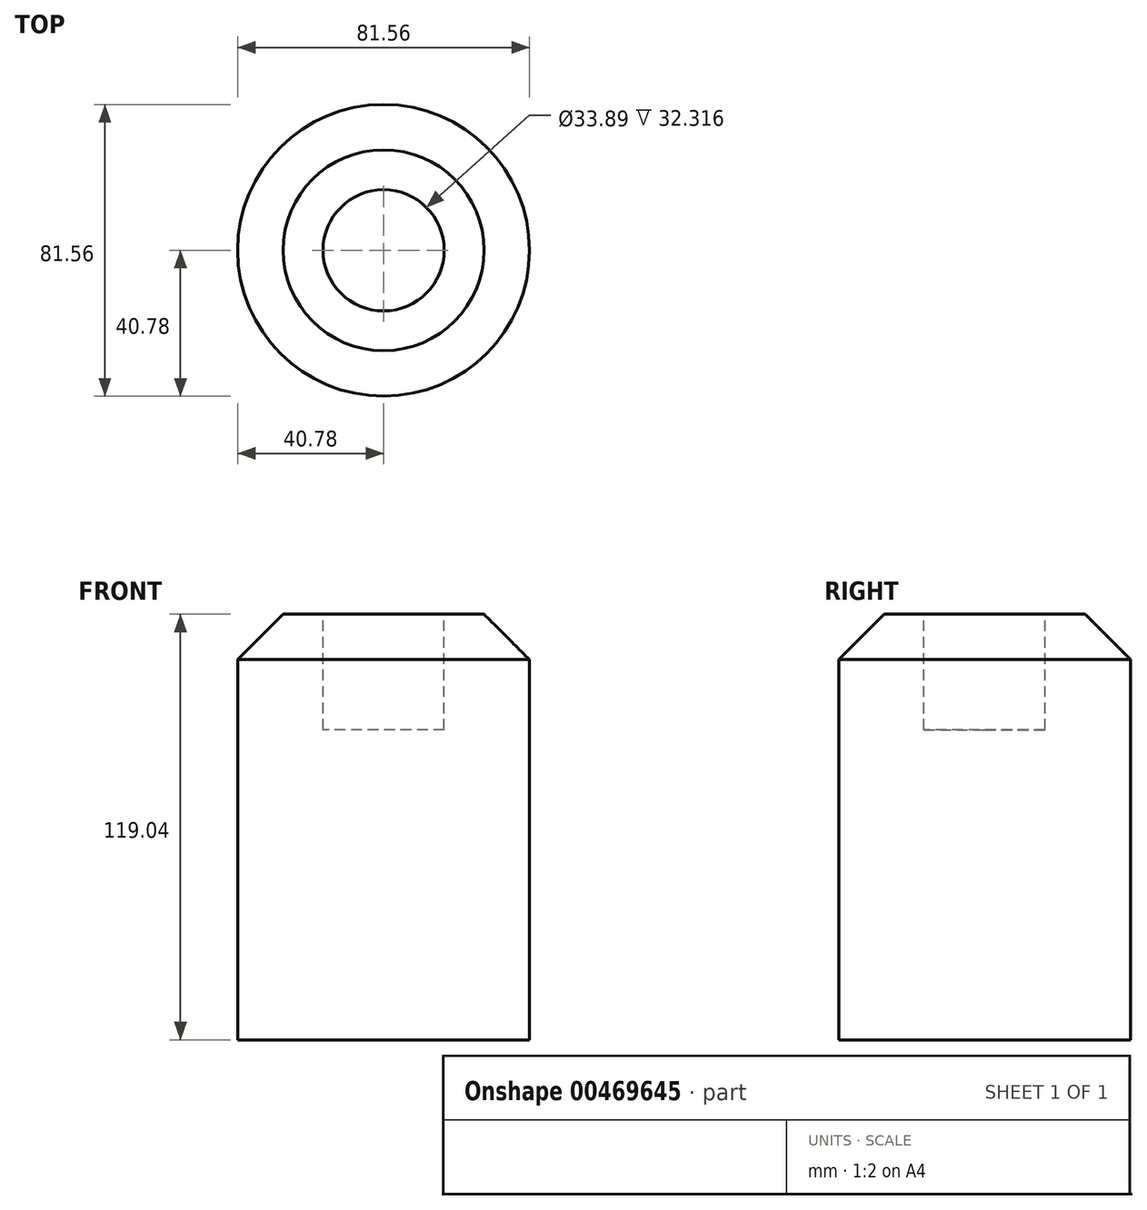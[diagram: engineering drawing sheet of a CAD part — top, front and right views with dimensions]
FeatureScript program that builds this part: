
annotation { "Feature Type Name" : "Feature", "Feature Type Description" : "" }
export const myFeature = defineFeature(function(context is Context, id is Id, definition is map)
    precondition{}
    {
        {
            var Q0;
            Q0=qCreatedBy(makeId("Top.planeOp"),FACE);
            var sketch = newSketch(context, id + "F0", { "sketchPlane" : qUnion([Q0])});
            skCircle(sketch, "E0", {"center": v(0, 0) * mm, "radius": 40.78 * mm});
            skSolve(sketch);
        }
        {
            var Q0;
            Q0=makeQuery(id+"F0.imprint","IMPRINT",FACE,{"disambiguationData":[TD([[makeQuery(id+"F0.imprint","IMPRINT",EDGE,{"derivedFrom":sQuery(id+"F0.wireOp",EDGE,"E0")}),1.0]])]});
            extrude(context, id + "F1", {"entities" : qUnion([Q0]), "depth" : 119.04 * mm});
        }
        {
            var Q0;
            Q0=qCreatedBy(makeId("Right.planeOp"),FACE);
            cPlane(context, id + "F2", {"entities" : qUnion([Q0]), "cplaneType" : CPlaneType.OFFSET, "offset" : 26.85 * mm, "width" : 152.4 * mm, "height" : 152.4 * mm});
        }
        {
            var Q0;
            Q0=makeQuery(id+"F1.opExtrude","CAP_FACE",FACE,{"disambiguationData":[OSD([sQuery(id+"F0.wireOp",EDGE,"E0")])],"isStart":false});
            var sketch = newSketch(context, id + "F3", { "sketchPlane" : qUnion([Q0])});
            skCircle(sketch, "E1", {"center": v(0, 0) * mm, "radius": 16.94 * mm});
            skSolve(sketch);
        }
        {
            var Q0;
            Q0=makeQuery(id+"F3.imprint","IMPRINT",FACE,{"disambiguationData":[TD([[makeQuery(id+"F3.imprint","IMPRINT",EDGE,{"derivedFrom":sQuery(id+"F3.wireOp",EDGE,"E1")}),1.0]])]});
            var Q1;
            Q1=sQuery(id+"F3.wireOp",EDGE,"E1");
            extrude(context, id + "F4", {"entities" : qUnion([Q0]), "operationType" : NewBodyOperationType.REMOVE, "surfaceEntities" : qUnion([Q1]), "oppositeDirection" : true, "depth" : 32.32 * mm});
        }
        {
            var Q0;
            Q0=makeQuery(id+"F1.opExtrude","CAP_EDGE",EDGE,{"disambiguationData":[OSD([sQuery(id+"F0.wireOp",EDGE,"E0")])],"isStart":false});
            chamfer(context, id + "F5", {"entities" : qUnion([Q0]), "width" : 12.7 * mm, "tangentPropagation" : true});
        }
    });
